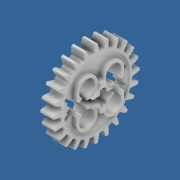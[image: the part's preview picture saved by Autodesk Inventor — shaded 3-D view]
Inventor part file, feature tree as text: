
AUTODESK INVENTOR PART (.ipt)
format: ipt  version: 2020 (Build 240168000, 168)  size: 1,657,856 bytes
history: mixed  units: mm
features: fillet x1, imported_body x1
ambient origin geometry x8: Origin, YZ Plane, XZ Plane, XY Plane, X Axis, Y Axis, Z Axis, Center Point
bodies: Solid1 (imported_parasolid)
feature tree (2):
  fillet  "Redondeo6"  [1 undecoded]
  imported_body  NMx_Import_Brep_tag  [imported B-rep: ~83 faces, bbox_mm=[4.0, 11.614208, 9.968773]]
note: 1 required parameter value undecoded (feature->parameter linkage not recoverable at this tier; creation-order binding heuristic only, values carry confidence <= 0.55)
